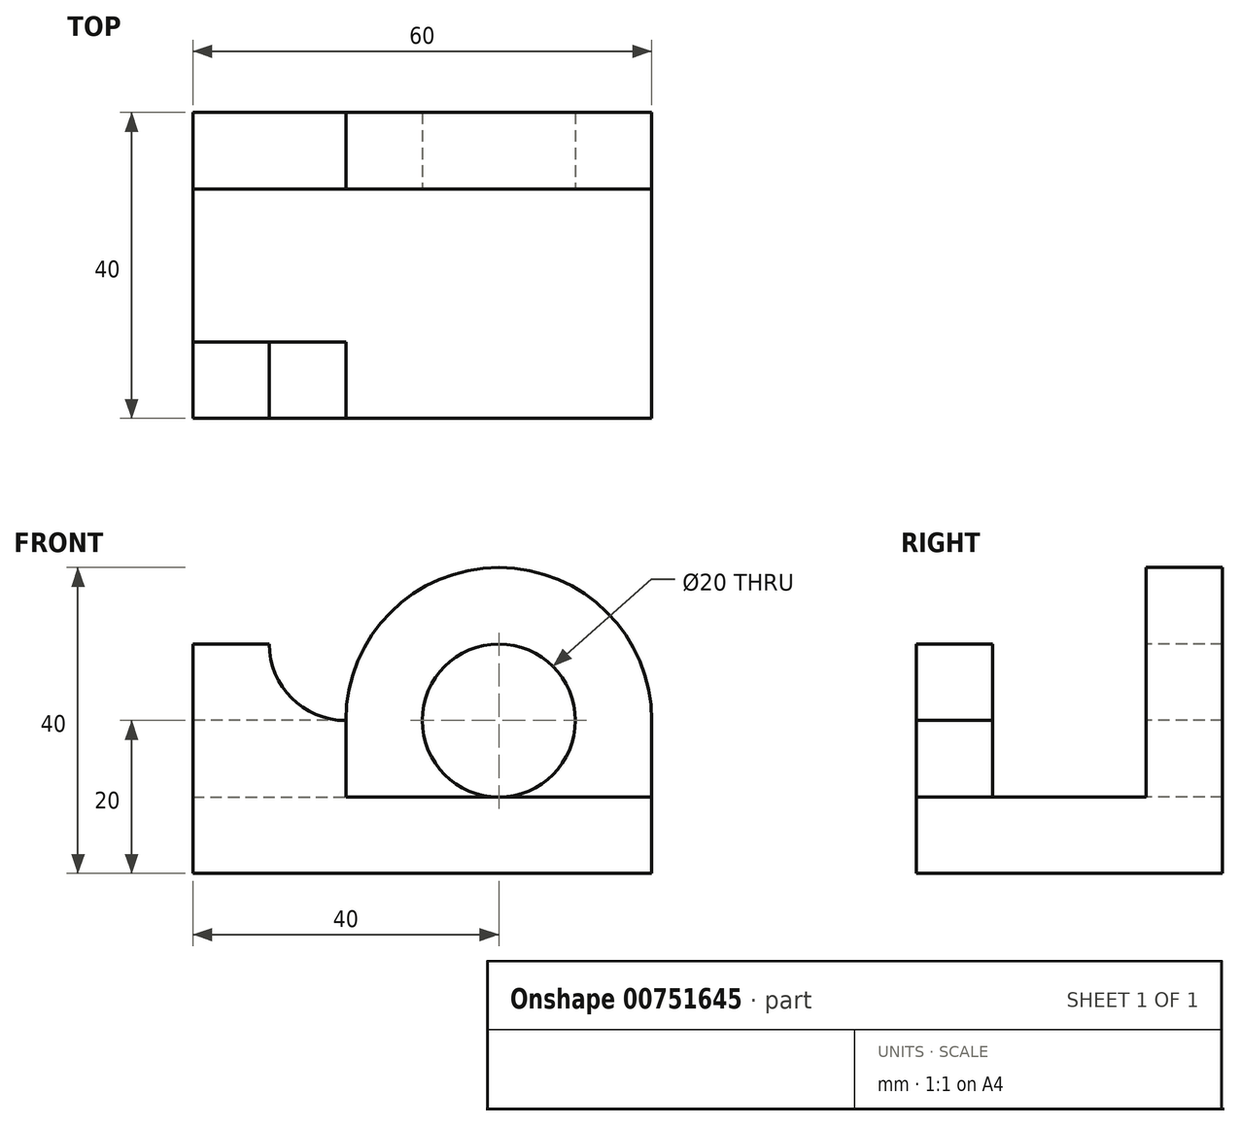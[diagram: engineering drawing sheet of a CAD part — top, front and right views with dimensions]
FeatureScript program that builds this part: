
annotation { "Feature Type Name" : "Feature", "Feature Type Description" : "" }
export const myFeature = defineFeature(function(context is Context, id is Id, definition is map)
    precondition{}
    {
        {
            var Q0;
            Q0=qCreatedBy(makeId("Top.planeOp"),FACE);
            var sketch = newSketch(context, id + "F0", { "sketchPlane" : qUnion([Q0])});
            skLineSegment(sketch, "E0.bottom", {"start": v(30, 20) * mm, "end": v(-30, 20) * mm});
            skLineSegment(sketch, "E0.top", {"start": v(30, -20) * mm, "end": v(-30, -20) * mm});
            skLineSegment(sketch, "E0.left", {"start": v(30, 20) * mm, "end": v(30, -20) * mm});
            skLineSegment(sketch, "E0.right", {"start": v(-30, 20) * mm, "end": v(-30, -20) * mm});
            skPoint(sketch, "E0.middle", {"position": v(0, 0) * mm});
            skSolve(sketch);
        }
        {
            var Q0;
            Q0=makeQuery(id+"F0.imprint","IMPRINT",FACE,{"disambiguationData":[TD([[makeQuery(id+"F0.imprint","IMPRINT",EDGE,{"derivedFrom":sQuery(id+"F0.wireOp",EDGE,"E0.bottom")}),1.0]])]});
            extrude(context, id + "F1", {"entities" : qUnion([Q0]), "depth" : 10 * mm, "offsetDistance" : 25 * mm});
        }
        {
            var Q0;
            Q0=makeQuery(id+"F1.opExtrude","CAP_FACE",FACE,{"disambiguationData":[OSD([sQuery(id+"F0.wireOp",EDGE,"E0.bottom"),sQuery(id+"F0.wireOp",EDGE,"E0.top"),sQuery(id+"F0.wireOp",EDGE,"E0.left"),sQuery(id+"F0.wireOp",EDGE,"E0.right")])],"isStart":false});
            var sketch = newSketch(context, id + "F2", { "sketchPlane" : qUnion([Q0])});
            skLineSegment(sketch, "E1.bottom", {"start": v(-30, 20) * mm, "end": v(30, 20) * mm});
            skLineSegment(sketch, "E1.top", {"start": v(-30, 10) * mm, "end": v(30, 10) * mm});
            skLineSegment(sketch, "E1.left", {"start": v(-30, 20) * mm, "end": v(-30, 10) * mm});
            skLineSegment(sketch, "E1.right", {"start": v(30, 20) * mm, "end": v(30, 10) * mm});
            skSolve(sketch);
        }
        {
            var Q0;
            Q0=makeQuery(id+"F2.imprint","IMPRINT",FACE,{"disambiguationData":[TD([[makeQuery(id+"F2.imprint","IMPRINT",EDGE,{"derivedFrom":sQuery(id+"F2.wireOp",EDGE,"E1.bottom")}),1.0]])]});
            extrude(context, id + "F3", {"entities" : qUnion([Q0]), "operationType" : NewBodyOperationType.ADD, "depth" : 10 * mm, "offsetDistance" : 25 * mm});
        }
        {
            var Q0;
            Q0=makeQuery(id+"F3.opExtrude","SWEPT_FACE",FACE,{"disambiguationData":[OSD([sQuery(id+"F2.wireOp",EDGE,"E1.top")])]});
            var sketch = newSketch(context, id + "F4", { "sketchPlane" : qUnion([Q0])});
            skArc(sketch, "E2", {"start": v(30, 20) * mm, "mid": v(10, 40) * mm, "end": v(-10, 20) * mm});
            skSolve(sketch);
        }
        {
            var Q0;
            {var subQ0=sQuery(id+"F4.wireOp",EDGE,"E2");Q0=makeQuery(id+"F4.imprint","IMPRINT",FACE,{"disambiguationData":[TD([[makeQuery(id+"F4.imprint","IMPRINT",EDGE,{"derivedFrom":subQ0}),1.0]])]});}
            extrude(context, id + "F5", {"entities" : qUnion([Q0]), "operationType" : NewBodyOperationType.ADD, "oppositeDirection" : true, "depth" : 10 * mm, "offsetDistance" : 25 * mm});
        }
        {
            var Q0;
            {var subQ0=sQuery(id+"F2.wireOp",EDGE,"E1.top");Q0=makeQuery(id+"F5.boolean.opBoolean","MERGE",FACE,{"derivedFrom":[makeQuery(id+"F3.opExtrude","SWEPT_FACE",FACE,{"disambiguationData":[OSD([subQ0])]}),makeQuery(id+"F5.opExtrude","CAP_FACE",FACE,{"disambiguationData":[OSD([subQ0,sQuery(id+"F4.wireOp",EDGE,"E2")])],"isStart":true})]});}
            var sketch = newSketch(context, id + "F6", { "sketchPlane" : qUnion([Q0])});
            skCircle(sketch, "E3", {"center": v(10, 20) * mm, "radius": 10 * mm});
            skPoint(sketch, "E3.first.point", {"position": v(10, 10) * mm});
            skPoint(sketch, "E3.second.point", {"position": v(11.11, 29.94) * mm});
            skPoint(sketch, "E3.third.point", {"position": v(4.49, 28.34) * mm});
            skSolve(sketch);
        }
        {
            var Q0;
            Q0=makeQuery(id+"F6.imprint","IMPRINT",FACE,{"disambiguationData":[TD([[makeQuery(id+"F6.imprint","IMPRINT",EDGE,{"derivedFrom":sQuery(id+"F6.wireOp",EDGE,"E3")}),1.0]])]});
            extrude(context, id + "F7", {"entities" : qUnion([Q0]), "operationType" : NewBodyOperationType.REMOVE, "oppositeDirection" : true, "depth" : 10 * mm, "offsetDistance" : 25 * mm});
        }
        {
            var Q0;
            Q0=makeQuery(id+"F1.opExtrude","CAP_FACE",FACE,{"disambiguationData":[OSD([sQuery(id+"F0.wireOp",EDGE,"E0.bottom"),sQuery(id+"F0.wireOp",EDGE,"E0.top"),sQuery(id+"F0.wireOp",EDGE,"E0.left"),sQuery(id+"F0.wireOp",EDGE,"E0.right")])],"isStart":false});
            var sketch = newSketch(context, id + "F8", { "sketchPlane" : qUnion([Q0])});
            skLineSegment(sketch, "E4.bottom", {"start": v(-30, -20) * mm, "end": v(-10, -20) * mm});
            skLineSegment(sketch, "E4.top", {"start": v(-30, -10) * mm, "end": v(-10, -10) * mm});
            skLineSegment(sketch, "E4.left", {"start": v(-30, -20) * mm, "end": v(-30, -10) * mm});
            skLineSegment(sketch, "E4.right", {"start": v(-10, -20) * mm, "end": v(-10, -10) * mm});
            skSolve(sketch);
        }
        {
            var Q0;
            Q0=makeQuery(id+"F8.imprint","IMPRINT",FACE,{"disambiguationData":[TD([[makeQuery(id+"F8.imprint","IMPRINT",EDGE,{"derivedFrom":sQuery(id+"F8.wireOp",EDGE,"E4.bottom")}),-1.0]])]});
            extrude(context, id + "F9", {"entities" : qUnion([Q0]), "operationType" : NewBodyOperationType.ADD, "depth" : 20 * mm, "offsetDistance" : 25 * mm});
        }
        {
            var Q0;
            Q0=makeQuery(id+"F9.boolean.opBoolean","MERGE",FACE,{"derivedFrom":[makeQuery(id+"F1.opExtrude","SWEPT_FACE",FACE,{"disambiguationData":[OSD([sQuery(id+"F0.wireOp",EDGE,"E0.top")])]}),makeQuery(id+"F9.opExtrude","SWEPT_FACE",FACE,{"disambiguationData":[OSD([sQuery(id+"F8.wireOp",EDGE,"E4.bottom")])]})]});
            var sketch = newSketch(context, id + "F10", { "sketchPlane" : qUnion([Q0])});
            skArc(sketch, "E5", {"start": v(-20, 30) * mm, "mid": v(-17.07, 22.93) * mm, "end": v(-10, 20) * mm});
            skSolve(sketch);
        }
        {
            var Q0;
            {var subQ0=sQuery(id+"F10.wireOp",EDGE,"E5");Q0=makeQuery(id+"F10.imprint","IMPRINT",FACE,{"disambiguationData":[TD([[makeQuery(id+"F10.imprint","IMPRINT",EDGE,{"derivedFrom":subQ0}),1.0]])]});}
            extrude(context, id + "F11", {"entities" : qUnion([Q0]), "operationType" : NewBodyOperationType.REMOVE, "oppositeDirection" : true, "depth" : 10 * mm, "offsetDistance" : 25 * mm});
        }
    });
